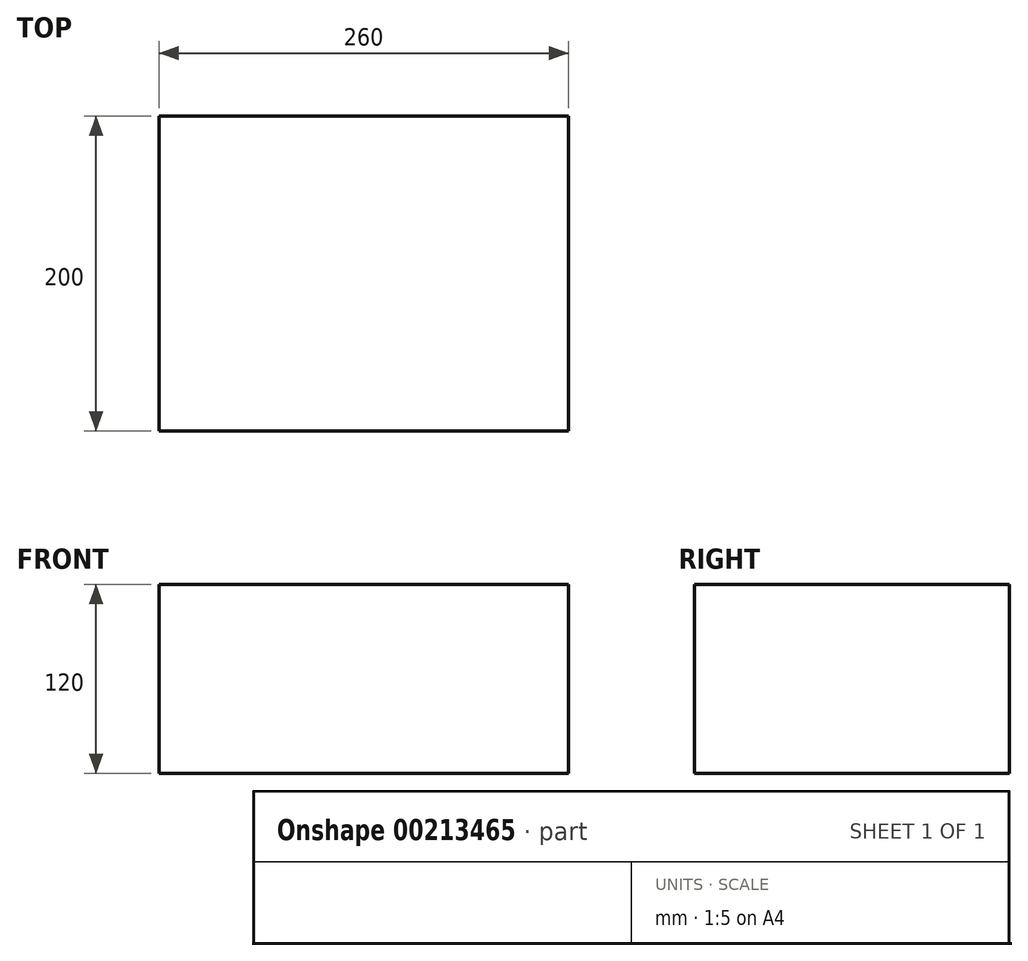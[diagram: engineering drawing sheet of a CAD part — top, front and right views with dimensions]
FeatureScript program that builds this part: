
annotation { "Feature Type Name" : "Feature", "Feature Type Description" : "" }
export const myFeature = defineFeature(function(context is Context, id is Id, definition is map)
    precondition{}
    {
        {
            var Q0;
            Q0=qCreatedBy(makeId("Top.planeOp"),FACE);
            var sketch = newSketch(context, id + "F0", { "sketchPlane" : qUnion([Q0])});
            skLineSegment(sketch, "E0.bottom", {"start": v(0, 0) * mm, "end": v(260, 0) * mm});
            skLineSegment(sketch, "E0.top", {"start": v(0, -200) * mm, "end": v(260, -200) * mm});
            skLineSegment(sketch, "E0.left", {"start": v(0, 0) * mm, "end": v(0, -200) * mm});
            skLineSegment(sketch, "E0.right", {"start": v(260, 0) * mm, "end": v(260, -200) * mm});
            skSolve(sketch);
        }
        {
            var Q0;
            Q0=makeQuery(id+"F0.imprint","IMPRINT",FACE,{"disambiguationData":[TD([[makeQuery(id+"F0.imprint","IMPRINT",EDGE,{"derivedFrom":sQuery(id+"F0.wireOp",EDGE,"E0.bottom")}),-1.0]])]});
            extrude(context, id + "F1", {"entities" : qUnion([Q0]), "depth" : 120 * mm});
        }
    });
